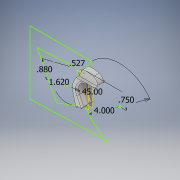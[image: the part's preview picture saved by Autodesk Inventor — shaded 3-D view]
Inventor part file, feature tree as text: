
AUTODESK INVENTOR PART (.ipt)
format: ipt  version: 2018.3 (Build 223284000, 284)  size: 256,000 bytes
history: native  units: in
note: dims shown in document units (in); Inventor stores cm internally (conversion verified against a paired STEP export)
features: extrude x4, sketch x3, plane x2, fillet x1
ambient origin geometry x8: Origin, YZ Plane, XZ Plane, XY Plane, X Axis, Y Axis, Z Axis, Center Point
bodies: Solid1 (feature_tree)
feature tree (10):
  sketch  "Sketch1"  dims[d1=0.5222in d2=0.426in]
  extrude  "Extrusion1"  Depth=0.426in
  extrude  "Extrusion2"  Depth=0.47in
  fillet  "Fillet1"  Radius=1.41in
  sketch  "Sketch3"  dims[d6=0.62in d7=0.22in d9=1.0in d10=0.75in d11=0.665in d12=0.1202in d13=1.563in d14=0.071in d15=0.124in d16=0.56in d17=0.0275in d18=0.841in d19=0.074in d20=0.428in d21=0.2096in d22=0.675in d23=0.255in d24=0.5222in d25=45.0deg d26=0.812in d27=0.73in d28=0.143in d29=0.619in d30=0.0in d32=0.309in d34=0.619in d35=0.0in d36=0.255in d37=0.0825in d38=0.75in d39=0.0in d40=4.0in d41=0.75in d42=45.0deg d43=0.527in d44=1.62in d45=0.88in d47=-0.276in d48=0.138in d49=0.0in d50=-0.149in d51=0.438in d52=0.0in]
  plane  "Work Plane2"
  extrude  "Extrusion3"  Depth=0.438in
  plane  "Work Plane3"
  extrude  "Extrusion4"  Depth=0.438in
  sketch  "Sketch2"  dims[d3=0.115in d4=0.47in d5=1.41in]
